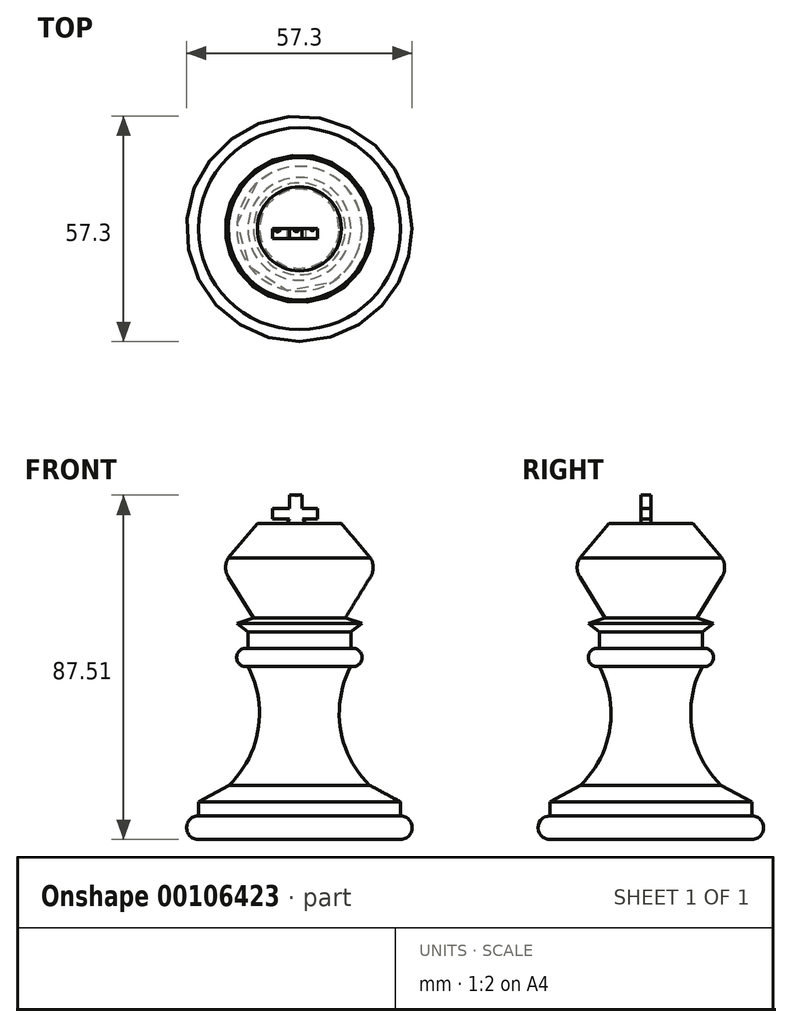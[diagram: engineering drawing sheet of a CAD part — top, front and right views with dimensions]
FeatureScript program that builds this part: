
annotation { "Feature Type Name" : "Feature", "Feature Type Description" : "" }
export const myFeature = defineFeature(function(context is Context, id is Id, definition is map)
    precondition{}
    {
        {
            var Q0;
            Q0=qCreatedBy(makeId("Front.planeOp"),FACE);
            var sketch = newSketch(context, id + "F0", { "sketchPlane" : qUnion([Q0])});
            skLineSegment(sketch, "E0", {"start": v(0, -43.96) * mm, "end": v(25.65, -43.96) * mm});
            skArc(sketch, "E1", {"start": v(25.65, -43.96) * mm, "mid": v(28.65, -40.97) * mm, "end": v(25.65, -37.97) * mm});
            skLineSegment(sketch, "E2", {"start": v(25.65, -37.97) * mm, "end": v(25.65, -34.38) * mm});
            skLineSegment(sketch, "E3", {"start": v(25.65, -34.38) * mm, "end": v(17.87, -30.18) * mm});
            skArc(sketch, "E4", {"start": v(13.07, 0) * mm, "mid": v(10.44, -15.9) * mm, "end": v(17.87, -30.18) * mm});
            skArc(sketch, "E5", {"start": v(13.07, 0) * mm, "mid": v(15.92, 2.28) * mm, "end": v(13.07, 4.56) * mm});
            skLineSegment(sketch, "E6", {"start": v(13.07, 4.56) * mm, "end": v(13.07, 8.76) * mm});
            skLineSegment(sketch, "E7", {"start": v(13.07, 8.76) * mm, "end": v(15.87, 10.95) * mm});
            skLineSegment(sketch, "E8", {"start": v(15.87, 10.95) * mm, "end": v(11.67, 12.35) * mm});
            skLineSegment(sketch, "E9", {"start": v(11.67, 12.35) * mm, "end": v(18.06, 22.74) * mm});
            skArc(sketch, "E10", {"start": v(18.06, 22.74) * mm, "mid": v(18.74, 25.13) * mm, "end": v(18.06, 27.53) * mm});
            skLineSegment(sketch, "E11", {"start": v(18.06, 27.53) * mm, "end": v(10.68, 36.32) * mm});
            skLineSegment(sketch, "E12", {"start": v(10.68, 36.32) * mm, "end": v(6.68, 36.32) * mm});
            skLineSegment(sketch, "E13", {"start": v(6.68, 36.32) * mm, "end": v(0, 36.32) * mm});
            skLineSegment(sketch, "E14", {"start": v(0, 36.32) * mm, "end": v(0, -43.96) * mm});
            skSolve(sketch);
        }
        {
            var Q0;
            Q0 = qSketchRegion(id + "F0", true);
            var Q1;
            Q1=sQuery(id+"F0.wireOp",EDGE,"E14");
            revolve(context, id + "F1", {"entities" : qUnion([Q0]), "axis" : qUnion([Q1]), "revolveType" : RevolveType.FULL});
        }
        {
            var Q0;
            Q0=qCreatedBy(makeId("Front.planeOp"),FACE);
            var sketch = newSketch(context, id + "F2", { "sketchPlane" : qUnion([Q0])});
            skLineSegment(sketch, "E15", {"start": v(0, 35.36) * mm, "end": v(1.47, 35.36) * mm});
            skLineSegment(sketch, "E16", {"start": v(1.47, 35.36) * mm, "end": v(2.36, 35.36) * mm});
            skLineSegment(sketch, "E17", {"start": v(2.36, 35.36) * mm, "end": v(0.85, 37.5) * mm});
            skLineSegment(sketch, "E18", {"start": v(0.85, 37.5) * mm, "end": v(4.59, 37.5) * mm});
            skLineSegment(sketch, "E19", {"start": v(4.59, 37.5) * mm, "end": v(4.59, 40.12) * mm});
            skLineSegment(sketch, "E20", {"start": v(4.59, 40.12) * mm, "end": v(0.72, 40.12) * mm});
            skLineSegment(sketch, "E21", {"start": v(0.72, 40.12) * mm, "end": v(0.72, 43.55) * mm});
            skLineSegment(sketch, "E22", {"start": v(0.72, 43.55) * mm, "end": v(-1.46, 43.55) * mm});
            skLineSegment(sketch, "E23", {"start": v(-1.46, 43.55) * mm, "end": v(-2.44, 43.55) * mm});
            skLineSegment(sketch, "E24", {"start": v(-2.44, 43.55) * mm, "end": v(-2.44, 40.12) * mm});
            skLineSegment(sketch, "E25", {"start": v(-2.44, 40.12) * mm, "end": v(-6.8, 40.12) * mm});
            skLineSegment(sketch, "E26", {"start": v(-6.8, 40.12) * mm, "end": v(-6.8, 37.5) * mm});
            skLineSegment(sketch, "E27", {"start": v(-6.8, 37.5) * mm, "end": v(-2.44, 37.5) * mm});
            skLineSegment(sketch, "E28", {"start": v(-2.44, 37.5) * mm, "end": v(-3.64, 35.36) * mm});
            skPoint(sketch, "E28.endSnap0", {"position": v(0.74, 35.36) * mm});
            skLineSegment(sketch, "E29", {"start": v(-3.64, 35.36) * mm, "end": v(0, 35.36) * mm});
            skSolve(sketch);
        }
        {
            var Q0;
            Q0 = qSketchRegion(id + "F2", true);
            extrude(context, id + "F3", {"entities" : qUnion([Q0]), "operationType" : NewBodyOperationType.ADD, "depth" : 2.47 * mm});
        }
        {
            var Q0;
            Q0=qCreatedBy(makeId("Front.planeOp"),FACE);
            var sketch = newSketch(context, id + "F4", { "sketchPlane" : qUnion([Q0])});
            skArc(sketch, "E30", {"start": v(-0.71, 43.39) * mm, "mid": v(0.3, 44.18) * mm, "end": v(-0.73, 44.96) * mm});
            skLineSegment(sketch, "E31", {"start": v(-0.73, 44.96) * mm, "end": v(-0.71, 43.39) * mm});
            skSolve(sketch);
        }
        {
            var Q0;
            Q0 = qSketchRegion(id + "F4", true);
            var Q1;
            Q1=sQuery(id+"F4.wireOp",EDGE,"E31");
            revolve(context, id + "F5", {"operationType" : NewBodyOperationType.ADD, "entities" : qUnion([Q0]), "axis" : qUnion([Q1]), "revolveType" : RevolveType.FULL});
        }
        {
            var Q0;
            Q0=qCreatedBy(makeId("Front.planeOp"),FACE);
            var sketch = newSketch(context, id + "F6", { "sketchPlane" : qUnion([Q0])});
            skArc(sketch, "E32", {"start": v(3.25, 40.07) * mm, "mid": v(4.58, 41.2) * mm, "end": v(3.29, 42.4) * mm});
            skLineSegment(sketch, "E33", {"start": v(3.29, 42.4) * mm, "end": v(3.25, 40.07) * mm});
            skSolve(sketch);
        }
        {
            var Q0;
            Q0=makeQuery(id+"F6.imprint","IMPRINT",FACE,{"disambiguationData":[TD([[makeQuery(id+"F6.imprint","IMPRINT",EDGE,{"derivedFrom":sQuery(id+"F6.wireOp",EDGE,"E32")}),1.0]])]});
            var Q1;
            Q1=sQuery(id+"F6.wireOp",EDGE,"E33");
            revolve(context, id + "F7", {"operationType" : NewBodyOperationType.ADD, "entities" : qUnion([Q0]), "axis" : qUnion([Q1]), "revolveType" : RevolveType.FULL});
        }
        {
            var Q0;
            Q0=qCreatedBy(makeId("Front.planeOp"),FACE);
            var sketch = newSketch(context, id + "F8", { "sketchPlane" : qUnion([Q0])});
            skArc(sketch, "E34", {"start": v(-5.55, 40.11) * mm, "mid": v(-4.12, 41.12) * mm, "end": v(-5.57, 42.1) * mm});
            skLineSegment(sketch, "E35", {"start": v(-5.57, 42.1) * mm, "end": v(-5.55, 40.11) * mm});
            skSolve(sketch);
        }
        {
            var Q0;
            Q0 = qSketchRegion(id + "F8", true);
            var Q1;
            Q1=sQuery(id+"F8.wireOp",EDGE,"E35");
            revolve(context, id + "F9", {"operationType" : NewBodyOperationType.ADD, "entities" : qUnion([Q0]), "axis" : qUnion([Q1]), "revolveType" : RevolveType.FULL});
        }
    });
